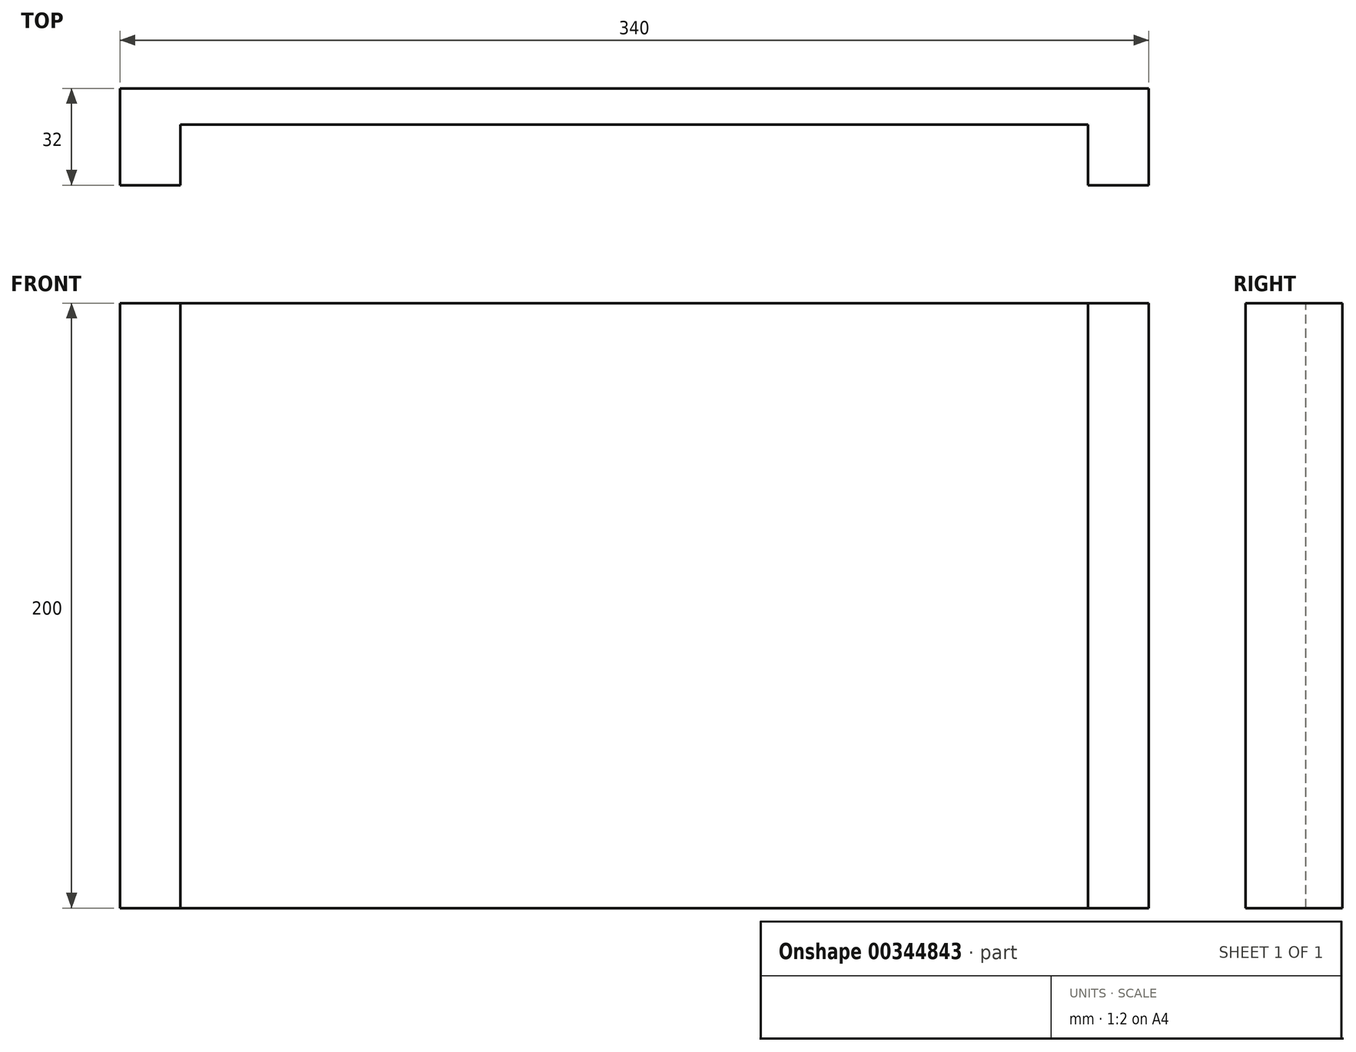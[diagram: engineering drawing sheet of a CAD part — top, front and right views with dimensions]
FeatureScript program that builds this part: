
annotation { "Feature Type Name" : "Feature", "Feature Type Description" : "" }
export const myFeature = defineFeature(function(context is Context, id is Id, definition is map)
    precondition{}
    {
        {
            var Q0;
            Q0=qCreatedBy(makeId("Right.planeOp"),FACE);
            var sketch = newSketch(context, id + "F0", { "sketchPlane" : qUnion([Q0])});
            skLineSegment(sketch, "E0.bottom", {"start": v(0, 0) * mm, "end": v(-12, 0) * mm});
            skLineSegment(sketch, "E0.top", {"start": v(0, 200) * mm, "end": v(-12, 200) * mm});
            skLineSegment(sketch, "E0.left", {"start": v(0, 0) * mm, "end": v(0, 200) * mm});
            skLineSegment(sketch, "E0.right", {"start": v(-12, 0) * mm, "end": v(-12, 200) * mm});
            skSolve(sketch);
        }
        {
            var Q0;
            Q0=makeQuery(id+"F0.imprint","IMPRINT",FACE,{"disambiguationData":[TD([[makeQuery(id+"F0.imprint","IMPRINT",EDGE,{"derivedFrom":sQuery(id+"F0.wireOp",EDGE,"E0.bottom")}),-1.0]])]});
            extrude(context, id + "F1", {"entities" : qUnion([Q0]), "depth" : 340 * mm});
        }
        {
            var Q0;
            Q0=makeQuery(id+"F1.opExtrude","SWEPT_FACE",FACE,{"disambiguationData":[OSD([sQuery(id+"F0.wireOp",EDGE,"E0.top")])]});
            var sketch = newSketch(context, id + "F2", { "sketchPlane" : qUnion([Q0])});
            skLineSegment(sketch, "E1.bottom", {"start": v(0, -12) * mm, "end": v(20, -12) * mm});
            skLineSegment(sketch, "E1.top", {"start": v(0, -32) * mm, "end": v(20, -32) * mm});
            skLineSegment(sketch, "E1.left", {"start": v(0, -12) * mm, "end": v(0, -32) * mm});
            skLineSegment(sketch, "E1.right", {"start": v(20, -12) * mm, "end": v(20, -32) * mm});
            skLineSegment(sketch, "E2.bottom", {"start": v(340, -12) * mm, "end": v(320, -12) * mm});
            skLineSegment(sketch, "E2.top", {"start": v(340, -32) * mm, "end": v(320, -32) * mm});
            skLineSegment(sketch, "E2.left", {"start": v(340, -12) * mm, "end": v(340, -32) * mm});
            skLineSegment(sketch, "E2.right", {"start": v(320, -12) * mm, "end": v(320, -32) * mm});
            skSolve(sketch);
        }
        {
            var Q0;
            Q0=makeQuery(id+"F2.imprint","IMPRINT",FACE,{"disambiguationData":[TD([[makeQuery(id+"F2.imprint","IMPRINT",EDGE,{"derivedFrom":sQuery(id+"F2.wireOp",EDGE,"E1.bottom")}),1.0]])]});
            var Q1;
            Q1=makeQuery(id+"F2.imprint","IMPRINT",FACE,{"disambiguationData":[TD([[makeQuery(id+"F2.imprint","IMPRINT",EDGE,{"derivedFrom":sQuery(id+"F2.wireOp",EDGE,"E2.bottom")}),1.0]])]});
            extrude(context, id + "F3", {"entities" : qUnion([Q0, Q1]), "operationType" : NewBodyOperationType.ADD, "oppositeDirection" : true, "depth" : 200 * mm});
        }
    });
